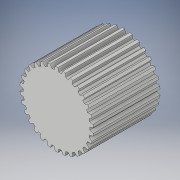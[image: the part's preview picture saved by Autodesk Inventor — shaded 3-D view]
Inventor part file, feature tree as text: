
AUTODESK INVENTOR PART (.ipt)
format: ipt  version: 2019 (Build 230136000, 136)  size: 285,184 bytes
history: native  units: in
note: dims shown in document units (in); Inventor stores cm internally (conversion verified against a paired STEP export)
features: extrude x1, sketch x1
ambient origin geometry x8: Origin, YZ Plane, XZ Plane, XY Plane, X Axis, Y Axis, Z Axis, Center Point
bodies: Solid1 (feature_tree)
feature tree (2):
  extrude  "Extrusion1"  Depth=1.0in
  sketch  "Sketch1"  dims[d0=1.0in d4=0.01in d5=0.01in d7=0.02in d9=75.0deg d12=105.0deg d13=11.811in d15=360.0deg d17=1.0in d18=0.0in]
